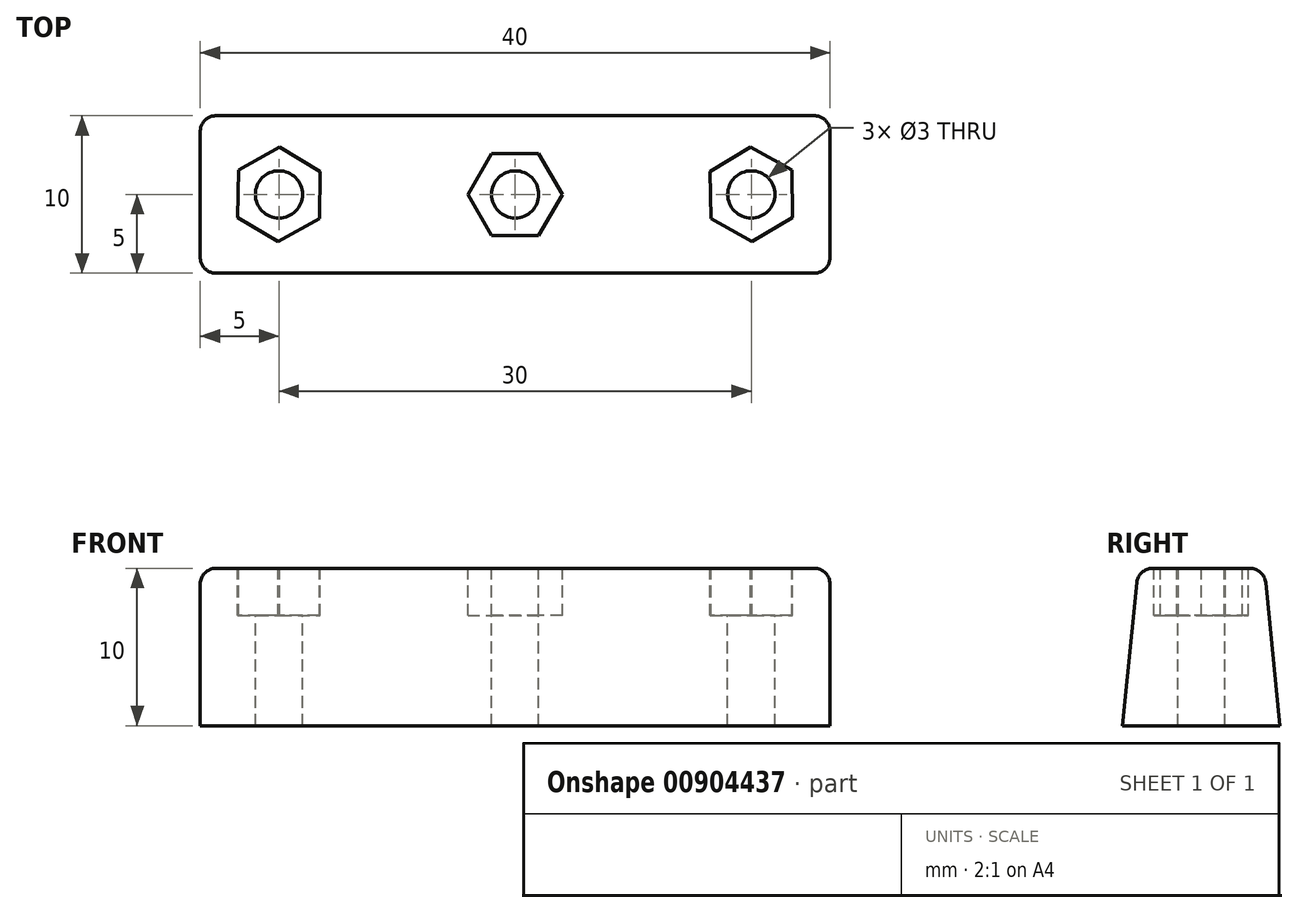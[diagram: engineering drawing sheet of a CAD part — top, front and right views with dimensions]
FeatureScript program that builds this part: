
annotation { "Feature Type Name" : "Feature", "Feature Type Description" : "" }
export const myFeature = defineFeature(function(context is Context, id is Id, definition is map)
    precondition{}
    {
        {
            var Q0;
            Q0=qCreatedBy(makeId("Right.planeOp"),FACE);
            var sketch = newSketch(context, id + "F0", { "sketchPlane" : qUnion([Q0])});
            skLineSegment(sketch, "E0", {"start": v(0, 0) * mm, "end": v(5, 0) * mm});
            skLineSegment(sketch, "E1", {"start": v(5, 0) * mm, "end": v(4.1, 9.1) * mm});
            skLineSegment(sketch, "E2", {"start": v(3.1, 10) * mm, "end": v(0, 10) * mm});
            skPoint(sketch, "E3.visualSharp", {"position": v(4, 10) * mm});
            skArc(sketch, "E3.filletArc", {"start": v(4.1, 9.1) * mm, "mid": v(3.77, 9.74) * mm, "end": v(3.1, 10) * mm});
            skArc(sketch, "E4.MirrorCS", {"start": v(-4.1, 9.1) * mm, "mid": v(-3.77, 9.74) * mm, "end": v(-3.1, 10) * mm});
            skLineSegment(sketch, "E5.MirrorCS", {"start": v(-5, 0) * mm, "end": v(-4.1, 9.1) * mm});
            skLineSegment(sketch, "E6.MirrorCS", {"start": v(0, 0) * mm, "end": v(-5, 0) * mm});
            skLineSegment(sketch, "E7.MirrorCS", {"start": v(-3.1, 10) * mm, "end": v(0, 10) * mm});
            skPoint(sketch, "E8.MirrorP", {"position": v(-4, 10) * mm});
            skSolve(sketch);
        }
        {
            var Q0;
            Q0 = qSketchRegion(id + "F0", true);
            extrude(context, id + "F1", {"entities" : qUnion([Q0]), "depth" : 20 * mm, "offsetDistance" : 25 * mm, "hasSecondDirection" : true, "secondDirectionOppositeDirection" : true, "secondDirectionDepth" : 20 * mm});
        }
        {
            var Q0;
            Q0=makeQuery(id+"F1.opExtrude","SWEPT_FACE",FACE,{"disambiguationData":[OSD([sQuery(id+"F0.wireOp",EDGE,"E2"),sQuery(id+"F0.wireOp",EDGE,"E7.MirrorCS")])]});
            var sketch = newSketch(context, id + "F2", { "sketchPlane" : qUnion([Q0])});
            skCircle(sketch, "E9", {"center": v(-15, 0) * mm, "radius": 1.5 * mm});
            skCircle(sketch, "E10.MirrorC", {"center": v(15, 0) * mm, "radius": 1.5 * mm});
            skCircle(sketch, "E11", {"center": v(0, 0) * mm, "radius": 1.5 * mm});
            skSolve(sketch);
        }
        {
            var Q0;
            Q0 = qSketchRegion(id + "F2", true);
            extrude(context, id + "F3", {"entities" : qUnion([Q0]), "operationType" : NewBodyOperationType.REMOVE, "endBound" : BoundingType.UP_TO_NEXT, "oppositeDirection" : true, "depth" : 25 * mm, "offsetDistance" : 25 * mm});
        }
        {
            var Q0;
            Q0=makeQuery(id+"F1.opExtrude","SWEPT_FACE",FACE,{"disambiguationData":[OSD([sQuery(id+"F0.wireOp",EDGE,"E2"),sQuery(id+"F0.wireOp",EDGE,"E7.MirrorCS")])]});
            var sketch = newSketch(context, id + "F4", { "sketchPlane" : qUnion([Q0])});
            skCircle(sketch, "E12.cCircle", {"center": v(-15, 0) * mm, "radius": 2.6 * mm, "construction": true});
            skLineSegment(sketch, "E12.0", {"start": v(-14.95, 3) * mm, "end": v(-12.37, 1.45) * mm});
            skLineSegment(sketch, "E12.1", {"start": v(-12.37, 1.45) * mm, "end": v(-12.43, -1.55) * mm});
            skLineSegment(sketch, "E12.2", {"start": v(-12.43, -1.55) * mm, "end": v(-15.05, -3) * mm});
            skLineSegment(sketch, "E12.3", {"start": v(-15.05, -3) * mm, "end": v(-17.63, -1.45) * mm});
            skLineSegment(sketch, "E12.4", {"start": v(-17.63, -1.45) * mm, "end": v(-17.57, 1.55) * mm});
            skLineSegment(sketch, "E12.5", {"start": v(-17.57, 1.55) * mm, "end": v(-14.95, 3) * mm});
            skPoint(sketch, "E12.0.midPoint", {"position": v(-13.66, 2.23) * mm});
            skLineSegment(sketch, "E13.MirrorCS", {"start": v(14.95, 3) * mm, "end": v(12.37, 1.45) * mm});
            skLineSegment(sketch, "E14.MirrorCS", {"start": v(17.57, 1.55) * mm, "end": v(14.95, 3) * mm});
            skLineSegment(sketch, "E15.MirrorCS", {"start": v(15.05, -3) * mm, "end": v(17.63, -1.45) * mm});
            skPoint(sketch, "E16.MirrorP", {"position": v(13.66, 2.23) * mm});
            skCircle(sketch, "E17.MirrorC", {"center": v(15, 0) * mm, "radius": 2.6 * mm, "construction": true});
            skLineSegment(sketch, "E18.MirrorCS", {"start": v(12.37, 1.45) * mm, "end": v(12.43, -1.55) * mm});
            skLineSegment(sketch, "E19.MirrorCS", {"start": v(12.43, -1.55) * mm, "end": v(15.05, -3) * mm});
            skLineSegment(sketch, "E20.MirrorCS", {"start": v(17.63, -1.45) * mm, "end": v(17.57, 1.55) * mm});
            skCircle(sketch, "E21.cCircle", {"center": v(0, 0) * mm, "radius": 2.6 * mm, "construction": true});
            skLineSegment(sketch, "E21.0", {"start": v(-1.5, 2.6) * mm, "end": v(1.5, 2.6) * mm});
            skLineSegment(sketch, "E21.1", {"start": v(1.5, 2.6) * mm, "end": v(3, 0) * mm});
            skLineSegment(sketch, "E21.2", {"start": v(3, 0) * mm, "end": v(1.5, -2.6) * mm});
            skLineSegment(sketch, "E21.3", {"start": v(1.5, -2.6) * mm, "end": v(-1.5, -2.6) * mm});
            skLineSegment(sketch, "E21.4", {"start": v(-1.5, -2.6) * mm, "end": v(-3, 0) * mm});
            skLineSegment(sketch, "E21.5", {"start": v(-3, 0) * mm, "end": v(-1.5, 2.6) * mm});
            skPoint(sketch, "E21.0.midPoint", {"position": v(0, 2.6) * mm});
            skSolve(sketch);
        }
        {
            var Q0;
            Q0 = qSketchRegion(id + "F4", true);
            extrude(context, id + "F5", {"entities" : qUnion([Q0]), "operationType" : NewBodyOperationType.REMOVE, "oppositeDirection" : true, "depth" : 3 * mm, "offsetDistance" : 25 * mm});
        }
        {
            var Q0;
            Q0=makeQuery(id+"F1.opExtrude","CAP_EDGE",EDGE,{"disambiguationData":[OSD([sQuery(id+"F0.wireOp",EDGE,"E2"),sQuery(id+"F0.wireOp",EDGE,"E7.MirrorCS")])],"isStart":false});
            fillet(context, id + "F6", {"entities" : qUnion([Q0]), "radius" : 1 * mm, "tangentPropagation" : true, "allowEdgeOverflow" : false});
        }
        {
            var Q0;
            Q0=makeQuery(id+"F1.opExtrude","CAP_EDGE",EDGE,{"disambiguationData":[OSD([sQuery(id+"F0.wireOp",EDGE,"E2"),sQuery(id+"F0.wireOp",EDGE,"E7.MirrorCS")])],"isStart":true});
            fillet(context, id + "F7", {"entities" : qUnion([Q0]), "radius" : 1 * mm, "tangentPropagation" : true, "allowEdgeOverflow" : false});
        }
    });
